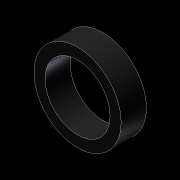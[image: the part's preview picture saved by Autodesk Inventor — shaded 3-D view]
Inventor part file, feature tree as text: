
AUTODESK INVENTOR PART (.ipt)
format: ipt  version: unknown  size: 161,280 bytes
history: native  units: in
note: dims shown in document units (in); Inventor stores cm internally (conversion verified against a paired STEP export)
features: extrude x1, sketch x1
ambient origin geometry x8: Origin, YZ Plane, XZ Plane, XY Plane, X Axis, Y Axis, Z Axis, Center Point
feature tree (2):
  extrude  "Extrusion1"  Depth=1.118in
  sketch  "Sketch1"  dims[d0=0.324in d1=0.0in d2=1.118in d3=0.834in]
